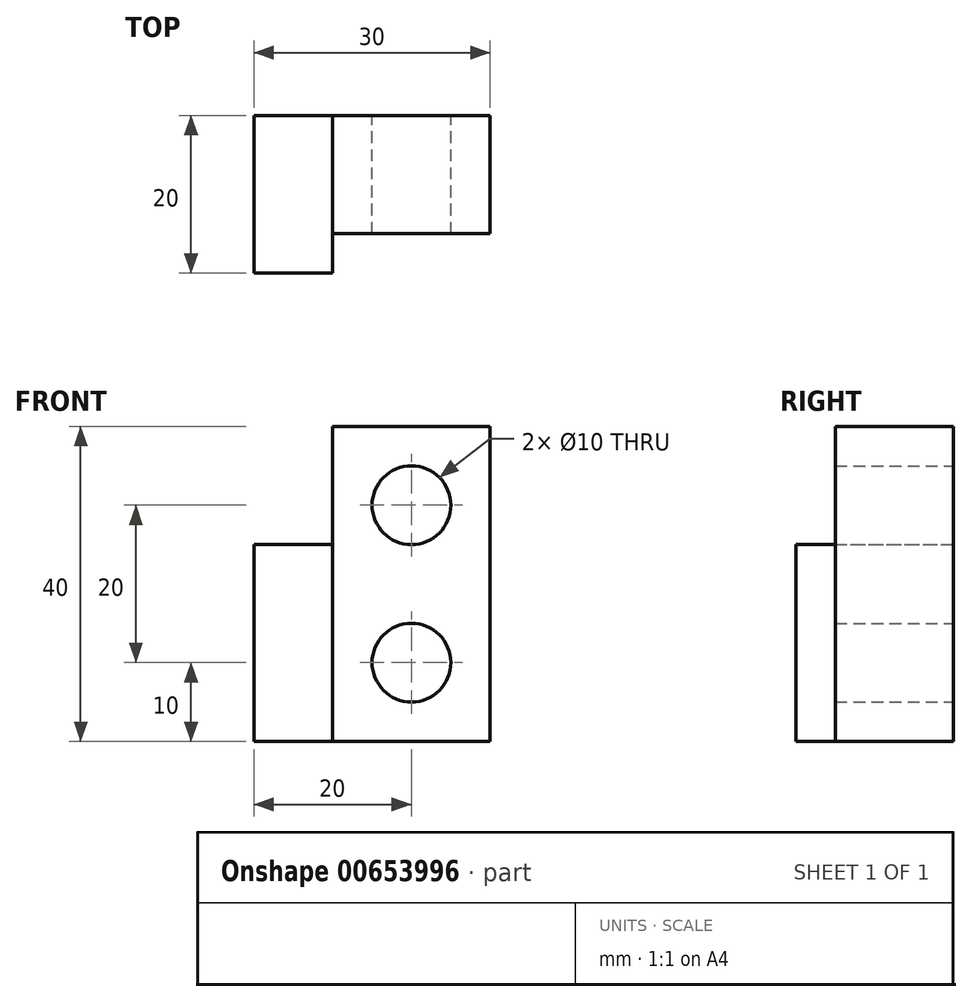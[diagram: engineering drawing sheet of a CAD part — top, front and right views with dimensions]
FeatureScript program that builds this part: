
annotation { "Feature Type Name" : "Feature", "Feature Type Description" : "" }
export const myFeature = defineFeature(function(context is Context, id is Id, definition is map)
    precondition{}
    {
        {
            var Q0;
            Q0=qCreatedBy(makeId("Front.planeOp"),FACE);
            var sketch = newSketch(context, id + "F0", { "sketchPlane" : qUnion([Q0])});
            skLineSegment(sketch, "E0.bottom", {"start": v(0, 0) * mm, "end": v(20, 0) * mm});
            skLineSegment(sketch, "E0.top", {"start": v(0, 40) * mm, "end": v(20, 40) * mm});
            skLineSegment(sketch, "E0.left", {"start": v(0, 0) * mm, "end": v(0, 40) * mm});
            skLineSegment(sketch, "E0.right", {"start": v(20, 0) * mm, "end": v(20, 40) * mm});
            skCircle(sketch, "E1", {"center": v(10, 30) * mm, "radius": 5 * mm});
            skCircle(sketch, "E2", {"center": v(10, 10) * mm, "radius": 5 * mm});
            skLineSegment(sketch, "E3.bottom", {"start": v(0, 0) * mm, "end": v(-10, 0) * mm});
            skLineSegment(sketch, "E3.top", {"start": v(0, 25) * mm, "end": v(-10, 25) * mm});
            skLineSegment(sketch, "E3.left", {"start": v(0, 0) * mm, "end": v(0, 25) * mm});
            skLineSegment(sketch, "E3.right", {"start": v(-10, 0) * mm, "end": v(-10, 25) * mm});
            skSolve(sketch);
        }
        {
            var Q0;
            Q0=makeQuery(id+"F0.imprint","IMPRINT",FACE,{"disambiguationData":[TD([[makeQuery(id+"F0.imprint","IMPRINT",EDGE,{"derivedFrom":sQuery(id+"F0.wireOp",EDGE,"E0.bottom")}),1.0]])]});
            extrude(context, id + "F1", {"entities" : qUnion([Q0]), "depth" : 15 * mm, "offsetDistance" : 25 * mm});
        }
        {
            var Q0;
            Q0=makeQuery(id+"F0.imprint","IMPRINT",FACE,{"disambiguationData":[TD([[makeQuery(id+"F0.imprint","IMPRINT",EDGE,{"derivedFrom":sQuery(id+"F0.wireOp",EDGE,"E3.bottom")}),-1.0]])]});
            extrude(context, id + "F2", {"entities" : qUnion([Q0]), "operationType" : NewBodyOperationType.ADD, "depth" : 20 * mm, "offsetDistance" : 25 * mm});
        }
    });
